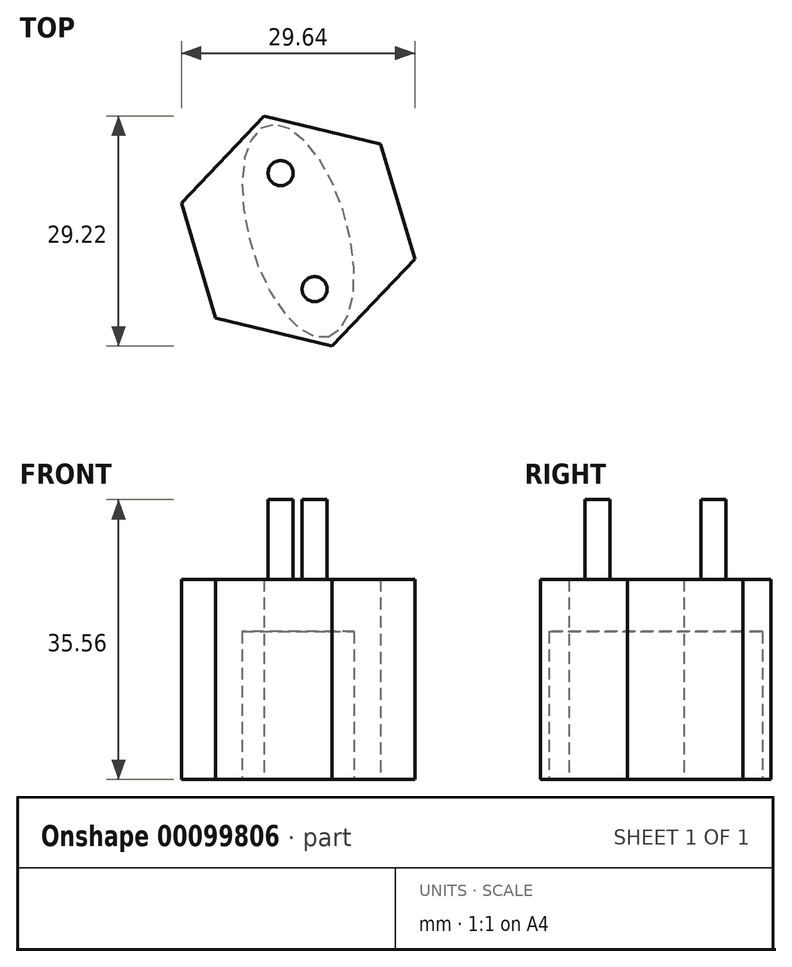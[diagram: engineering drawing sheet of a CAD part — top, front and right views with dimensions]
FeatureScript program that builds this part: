
annotation { "Feature Type Name" : "Feature", "Feature Type Description" : "" }
export const myFeature = defineFeature(function(context is Context, id is Id, definition is map)
    precondition{}
    {
        {
            var Q0;
            Q0=qCreatedBy(makeId("Top.planeOp"),FACE);
            var sketch = newSketch(context, id + "F0", { "sketchPlane" : qUnion([Q0])});
            skCircle(sketch, "E0.cCircle", {"center": v(0, 0) * mm, "radius": 13.2 * mm, "construction": true});
            skLineSegment(sketch, "E0.0", {"start": v(14.82, -3.57) * mm, "end": v(4.32, -14.61) * mm});
            skLineSegment(sketch, "E0.1", {"start": v(4.32, -14.61) * mm, "end": v(-10.5, -11.05) * mm});
            skLineSegment(sketch, "E0.2", {"start": v(-10.5, -11.05) * mm, "end": v(-14.82, 3.57) * mm});
            skLineSegment(sketch, "E0.3", {"start": v(-14.82, 3.57) * mm, "end": v(-4.32, 14.61) * mm});
            skLineSegment(sketch, "E0.4", {"start": v(-4.32, 14.61) * mm, "end": v(10.5, 11.05) * mm});
            skLineSegment(sketch, "E0.5", {"start": v(10.5, 11.05) * mm, "end": v(14.82, -3.57) * mm});
            skPoint(sketch, "E0.0.midPoint", {"position": v(9.57, -9.1) * mm});
            skSolve(sketch);
        }
        {
            var Q0;
            Q0=makeQuery(id+"F0.imprint","IMPRINT",FACE,{"disambiguationData":[TD([[makeQuery(id+"F0.imprint","IMPRINT",EDGE,{"derivedFrom":sQuery(id+"F0.wireOp",EDGE,"E0.0")}),-1.0]])]});
            var sketch = newSketch(context, id + "F1", { "sketchPlane" : qUnion([Q0])});
            skEllipse(sketch, "E1", {"center": v(0, 0) * mm, "majorRadius": 13.97 * mm, "minorRadius": 6.23 * mm, "majorAxis": v(0.28, -0.96)});
            skSolve(sketch);
        }
        {
            var Q0;
            Q0=makeQuery(id+"F0.imprint","IMPRINT",FACE,{"disambiguationData":[TD([[makeQuery(id+"F0.imprint","IMPRINT",EDGE,{"derivedFrom":sQuery(id+"F0.wireOp",EDGE,"E0.0")}),-1.0]])]});
            extrude(context, id + "F2", {"entities" : qUnion([Q0]), "depth" : 25.4 * mm});
        }
        {
            var Q0;
            Q0=makeQuery(id+"F1.imprint","IMPRINT",FACE,{"disambiguationData":[TD([[makeQuery(id+"F1.imprint","IMPRINT",EDGE,{"derivedFrom":sQuery(id+"F1.wireOp",EDGE,"E1")}),1.0]])]});
            extrude(context, id + "F3", {"entities" : qUnion([Q0]), "operationType" : NewBodyOperationType.REMOVE, "depth" : 18.8 * mm});
        }
        {
            var Q0;
            Q0=makeQuery(id+"F2.opExtrude","CAP_FACE",FACE,{"disambiguationData":[OSD([sQuery(id+"F0.wireOp",EDGE,"E0.0"),sQuery(id+"F0.wireOp",EDGE,"E0.1"),sQuery(id+"F0.wireOp",EDGE,"E0.2"),sQuery(id+"F0.wireOp",EDGE,"E0.3"),sQuery(id+"F0.wireOp",EDGE,"E0.4"),sQuery(id+"F0.wireOp",EDGE,"E0.5")])],"isStart":false});
            var sketch = newSketch(context, id + "F4", { "sketchPlane" : qUnion([Q0])});
            skCircle(sketch, "E2", {"center": v(-2.22, 7.36) * mm, "radius": 1.59 * mm});
            skSolve(sketch);
        }
        {
            var Q0;
            Q0=makeQuery(id+"F4.imprint","IMPRINT",FACE,{"disambiguationData":[TD([[makeQuery(id+"F4.imprint","IMPRINT",EDGE,{"derivedFrom":sQuery(id+"F4.wireOp",EDGE,"E2")}),-1.0]])]});
            var sketch = newSketch(context, id + "F5", { "sketchPlane" : qUnion([Q0])});
            skCircle(sketch, "E3", {"center": v(2.1, -7.4) * mm, "radius": 1.59 * mm});
            skSolve(sketch);
        }
        {
            var Q0;
            Q0=makeQuery(id+"F4.imprint","IMPRINT",FACE,{"disambiguationData":[TD([[makeQuery(id+"F4.imprint","IMPRINT",EDGE,{"derivedFrom":sQuery(id+"F4.wireOp",EDGE,"E2")}),1.0]])]});
            extrude(context, id + "F6", {"entities" : qUnion([Q0]), "operationType" : NewBodyOperationType.ADD, "depth" : 10.16 * mm});
        }
        {
            var Q0;
            Q0=makeQuery(id+"F5.imprint","IMPRINT",FACE,{"disambiguationData":[TD([[makeQuery(id+"F5.imprint","IMPRINT",EDGE,{"derivedFrom":sQuery(id+"F5.wireOp",EDGE,"E3")}),1.0]])]});
            extrude(context, id + "F7", {"entities" : qUnion([Q0]), "operationType" : NewBodyOperationType.ADD, "depth" : 10.16 * mm});
        }
    });
